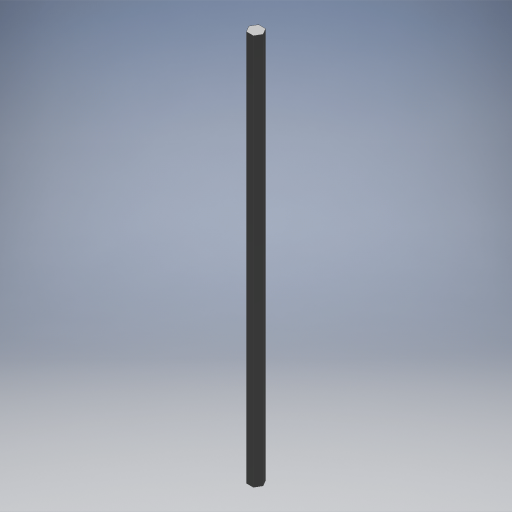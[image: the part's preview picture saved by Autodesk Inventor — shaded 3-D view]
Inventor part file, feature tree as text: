
AUTODESK INVENTOR PART (.ipt)
format: ipt  version: 2024.2 (Build 282272000, 272)  size: 450,560 bytes
history: native  units: in
note: dims shown in document units (in); Inventor stores cm internally (conversion verified against a paired STEP export)
features: extrude x32, other x4, hole x2
ambient origin geometry x8: Origin, YZ Plane, XZ Plane, XY Plane, X Axis, Y Axis, Z Axis, Center Point
bodies: Solid3 (feature_tree)
feature tree (38):
  extrude  "BaseProfile625Round"  Depth=0.5in
  extrude  "BaseProfileRoundTube"  Depth=0.5413in
  extrude  "BaseProfile500Hex"  Depth=0.5in
  extrude  "BaseProfile500Thunderhex"  Depth=0.375in
  extrude  "BaseProfile500Round"  Depth=0.4035in
  extrude  "BaseProfile375Hex"  Depth=0.75in
  extrude  "BaseProfile375Thunderhex"  Depth=0.468in
  extrude  "BaseProfile375Round"  Depth=0.201in
  extrude  "TopShaftProfile1Hex500"  Depth=0.159in
  extrude  "TopShaftProfile1ThunderHex500"  Depth=0.25in
  extrude  "TopShaftProfile1Round500"  Depth=36.0in TaperAngle=0.0deg
  extrude  "TopShaftProfile1Hex375"  Depth=16.0in TaperAngle=0.0deg
  extrude  "TopShaftProfile1ThunderHex375"  Depth=36.0in TaperAngle=0.0deg
  extrude  "TopShaftProfile1Round375"  Depth=36.0in TaperAngle=0.0deg
  extrude  "TopShaftProfile2ThunderHex500"  Depth=36.0in TaperAngle=0.0deg
  extrude  "TopShaftProfile2Round500"  Depth=36.0in TaperAngle=0.0deg
  extrude  "TopShaftProfile2Hex375"  Depth=36.0in TaperAngle=0.0deg
  extrude  "TopShaftProfile2ThunderHex375"  Depth=36.0in TaperAngle=0.0deg
  extrude  "TopShaftProfile2Round375"  Depth=36.0in TaperAngle=0.0deg
  other  "TopRetentionGroove&BearingRound"
  hole  "TopShaftTappedHole"  [1 undecoded]
  other  "TopShaftThread"
  extrude  "BottomShaftProfile1Hex500"  TaperAngle=0.0deg  [1 undecoded]
  extrude  "BottomShaftProfile1ThunderHex500"  TaperAngle=0.0deg  [1 undecoded]
  extrude  "BottomShaftProfile1Round500"  TaperAngle=0.0deg  [1 undecoded]
  extrude  "BottomShaftProfile1Hex375"  TaperAngle=0.0deg  [1 undecoded]
  extrude  "BottomShaftProfile1ThunderHex375"  TaperAngle=0.0deg  [1 undecoded]
  extrude  "BottomShaftProfile2ThunderHex500"  TaperAngle=0.0deg  [1 undecoded]
  extrude  "BottomShaftProfile1Round375"  TaperAngle=0.0deg  [1 undecoded]
  extrude  "BottomShaftProfile2Round500"  TaperAngle=0.0deg  [1 undecoded]
  extrude  "BottomShaftProfile2Hex375"  TaperAngle=0.0deg  [1 undecoded]
  extrude  "BottomShaftProfile2ThunderHex375"  TaperAngle=0.0deg  [1 undecoded]
  extrude  "BottomShaftProfile2Round375"  TaperAngle=0.0deg  [1 undecoded]
  hole  "BottomShaftTappedHole"  [1 undecoded]
  other  "BottomShaftThread"
  other  "BottomRetentionGroove&BearingRound"
  extrude  "BaseProfile375ThunderhexHole"  TaperAngle=0.0deg  [1 undecoded]
  extrude  "BaseProfile500ThunderhexHole"  TaperAngle=0.0deg  [1 undecoded]
note: 15 required parameter values undecoded (feature->parameter linkage not recoverable at this tier; creation-order binding heuristic only, values carry confidence <= 0.55)
